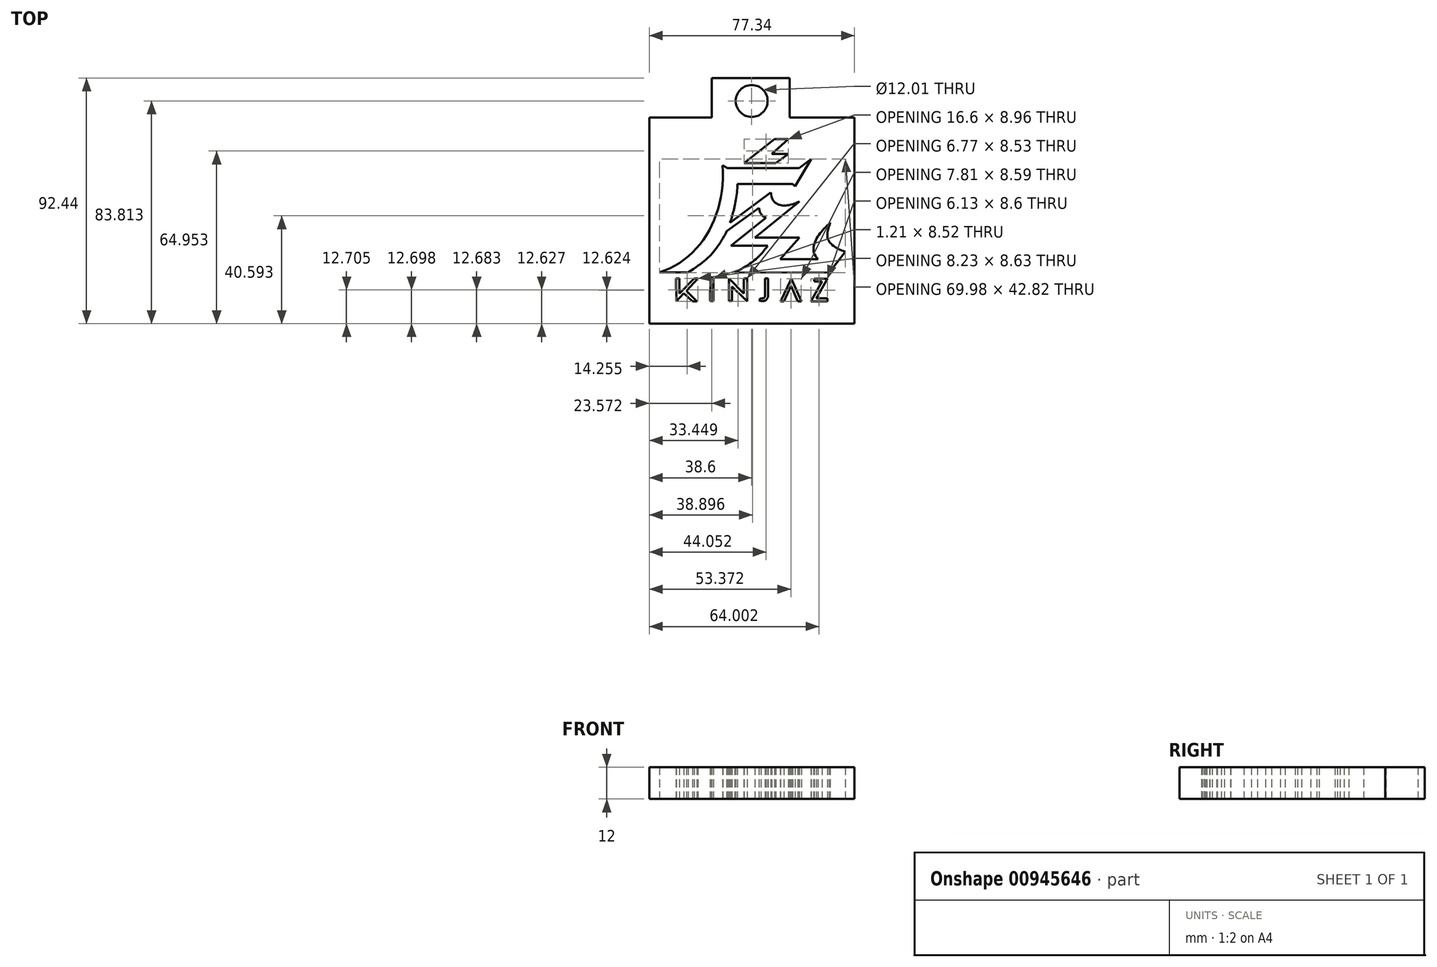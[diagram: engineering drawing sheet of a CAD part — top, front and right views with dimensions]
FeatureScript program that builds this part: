
annotation { "Feature Type Name" : "Feature", "Feature Type Description" : "" }
export const myFeature = defineFeature(function(context is Context, id is Id, definition is map)
    precondition{}
    {
        {
            var Q0;
            Q0=qCreatedBy(makeId("Top.planeOp"),FACE);
            var sketch = newSketch(context, id + "F0", { "sketchPlane" : qUnion([Q0])});
            skLineSegment(sketch, "E0", {"start": v(-62.68, -21.2) * mm, "end": v(-73.43, -21.2) * mm});
            skFitSpline(sketch, "E1", {"points": [v(-73.43, -21.2) * mm, v(-49.68, 19) * mm], "startDerivative": vector(47.19, 15.16) * mm, "endDerivative": vector(-3.26, 57) * mm});
            skLineSegment(sketch, "E2", {"start": v(-49.68, 19) * mm, "end": v(-47.8, 18.08) * mm});
            skLineSegment(sketch, "E3", {"start": v(-47.8, 18.08) * mm, "end": v(-20.92, 18.08) * mm});
            skLineSegment(sketch, "E4", {"start": v(-20.92, 18.08) * mm, "end": v(-16.26, 21.48) * mm});
            skLineSegment(sketch, "E5", {"start": v(-16.26, 21.48) * mm, "end": v(-22.39, 11.17) * mm});
            skLineSegment(sketch, "E6", {"start": v(-22.39, 11.17) * mm, "end": v(-23.32, 12.08) * mm});
            skLineSegment(sketch, "E7", {"start": v(-23.32, 12.08) * mm, "end": v(-44.1, 12.08) * mm});
            skFitSpline(sketch, "E8", {"points": [v(-44.1, 12.08) * mm, v(-46.88, -2.52) * mm], "startDerivative": vector(-0.62, -19.4) * mm, "endDerivative": vector(-2.9, -9.08) * mm});
            skLineSegment(sketch, "E9", {"start": v(-46.88, -2.52) * mm, "end": v(-31.55, 8.9) * mm});
            skFitSpline(sketch, "E10", {"points": [v(-31.55, 8.9) * mm, v(-20.72, 5.45) * mm], "startDerivative": vector(1, -17.55) * mm, "endDerivative": vector(15.07, 7.4) * mm});
            skLineSegment(sketch, "E11", {"start": v(-20.72, 5.45) * mm, "end": v(-37.54, -8.14) * mm});
            skLineSegment(sketch, "E12", {"start": v(-37.54, -8.14) * mm, "end": v(-20.72, -8.14) * mm});
            skLineSegment(sketch, "E13", {"start": v(-20.72, -8.14) * mm, "end": v(-27.98, -16.25) * mm});
            skLineSegment(sketch, "E14", {"start": v(-27.98, -16.25) * mm, "end": v(-13.84, -16.24) * mm});
            skFitSpline(sketch, "E15", {"points": [v(-13.84, -16.24) * mm, v(-9.18, -2.48) * mm], "startDerivative": vector(-12.1, 12.63) * mm, "endDerivative": vector(13.54, 12.46) * mm});
            skFitSpline(sketch, "E16", {"points": [v(-9.18, -2.48) * mm, v(-3.46, -13.46) * mm], "startDerivative": vector(-3.73, -12.22) * mm, "endDerivative": vector(26.55, -9.04) * mm});
            skLineSegment(sketch, "E17", {"start": v(-3.46, -13.46) * mm, "end": v(-9.55, -21.33) * mm});
            skLineSegment(sketch, "E18", {"start": v(-9.55, -21.33) * mm, "end": v(-45.15, -21.17) * mm});
            skFitSpline(sketch, "E19", {"points": [v(-45.15, -21.17) * mm, v(-32.64, -11.13) * mm], "startDerivative": vector(11.27, 5.6) * mm, "endDerivative": vector(13.15, 18.44) * mm});
            skLineSegment(sketch, "E20", {"start": v(-32.64, -11.13) * mm, "end": v(-46.53, -11.13) * mm});
            skLineSegment(sketch, "E21", {"start": v(-46.53, -11.13) * mm, "end": v(-33.3, -0.7) * mm});
            skFitSpline(sketch, "E22", {"points": [v(-35.96, 3.08) * mm, v(-33.3, -0.7) * mm], "startDerivative": vector(0.57, -2.62) * mm, "endDerivative": vector(7.97, -3.11) * mm});
            skLineSegment(sketch, "E23", {"start": v(-35.96, 3.08) * mm, "end": v(-48.13, -5.8) * mm});
            skFitSpline(sketch, "E24", {"points": [v(-48.13, -5.8) * mm, v(-62.68, -21.2) * mm], "startDerivative": vector(-11.33, -21.28) * mm, "endDerivative": vector(-24.18, -14.95) * mm});
            skLineSegment(sketch, "E25", {"start": v(-41.6, 19.95) * mm, "end": v(-29.66, 19.95) * mm});
            skLineSegment(sketch, "E26", {"start": v(-29.66, 19.95) * mm, "end": v(-24.99, 23.3) * mm});
            skLineSegment(sketch, "E27", {"start": v(-24.99, 23.3) * mm, "end": v(-31.19, 23.3) * mm});
            skLineSegment(sketch, "E28", {"start": v(-31.19, 23.3) * mm, "end": v(-24.99, 28.91) * mm});
            skLineSegment(sketch, "E29", {"start": v(-24.99, 28.91) * mm, "end": v(-30.1, 28.91) * mm});
            skLineSegment(sketch, "E30", {"start": v(-30.1, 28.91) * mm, "end": v(-41.6, 19.95) * mm});
            skLineSegment(sketch, "E31", {"start": v(-67.2, -23.56) * mm, "end": v(-66.02, -23.56) * mm});
            skLineSegment(sketch, "E32", {"start": v(-66.02, -23.56) * mm, "end": v(-66.02, -29.19) * mm});
            skLineSegment(sketch, "E33", {"start": v(-66.02, -29.19) * mm, "end": v(-60.45, -23.52) * mm});
            skLineSegment(sketch, "E34", {"start": v(-60.45, -23.52) * mm, "end": v(-58.97, -23.52) * mm});
            skLineSegment(sketch, "E35", {"start": v(-58.97, -23.52) * mm, "end": v(-63.34, -28.2) * mm});
            skLineSegment(sketch, "E36", {"start": v(-63.34, -28.2) * mm, "end": v(-59.36, -32.15) * mm});
            skLineSegment(sketch, "E37", {"start": v(-59.36, -32.15) * mm, "end": v(-61.02, -32.15) * mm});
            skLineSegment(sketch, "E38", {"start": v(-61.02, -32.15) * mm, "end": v(-64.27, -29.08) * mm});
            skLineSegment(sketch, "E39", {"start": v(-64.27, -29.08) * mm, "end": v(-67.16, -32.13) * mm});
            skLineSegment(sketch, "E40", {"start": v(-67.16, -32.13) * mm, "end": v(-67.2, -23.56) * mm});
            skLineSegment(sketch, "E41", {"start": v(-54.3, -23.56) * mm, "end": v(-53.16, -23.56) * mm});
            skLineSegment(sketch, "E42", {"start": v(-53.16, -23.56) * mm, "end": v(-53.16, -32.07) * mm});
            skLineSegment(sketch, "E43", {"start": v(-53.16, -32.07) * mm, "end": v(-54.37, -32.07) * mm});
            skLineSegment(sketch, "E44", {"start": v(-54.37, -32.07) * mm, "end": v(-54.3, -23.56) * mm});
            skLineSegment(sketch, "E45", {"start": v(-47.28, -32.07) * mm, "end": v(-46.14, -32.07) * mm});
            skLineSegment(sketch, "E46", {"start": v(-46.14, -32.07) * mm, "end": v(-46.14, -26.55) * mm});
            skLineSegment(sketch, "E47", {"start": v(-46.14, -26.55) * mm, "end": v(-40.5, -32.09) * mm});
            skLineSegment(sketch, "E48", {"start": v(-40.5, -32.09) * mm, "end": v(-40.5, -23.56) * mm});
            skLineSegment(sketch, "E49", {"start": v(-40.5, -23.56) * mm, "end": v(-41.7, -23.56) * mm});
            skLineSegment(sketch, "E50", {"start": v(-41.7, -23.56) * mm, "end": v(-41.7, -29.19) * mm});
            skLineSegment(sketch, "E51", {"start": v(-41.7, -29.19) * mm, "end": v(-47.25, -23.56) * mm});
            skLineSegment(sketch, "E52", {"start": v(-47.25, -23.56) * mm, "end": v(-47.28, -32.07) * mm});
            skFitSpline(sketch, "E53", {"points": [v(-35.95, -31.8) * mm, v(-32.6, -30.5) * mm], "startDerivative": vector(7.27, -2.05) * mm, "endDerivative": vector(1.5, 3.19) * mm});
            skLineSegment(sketch, "E54", {"start": v(-32.6, -30.5) * mm, "end": v(-32.6, -23.54) * mm});
            skLineSegment(sketch, "E55", {"start": v(-32.6, -23.54) * mm, "end": v(-33.72, -23.54) * mm});
            skLineSegment(sketch, "E56", {"start": v(-33.72, -23.54) * mm, "end": v(-33.72, -30.23) * mm});
            skFitSpline(sketch, "E57", {"points": [v(-33.72, -30.23) * mm, v(-35.23, -30.94) * mm], "startDerivative": vector(-0.8, -2.46) * mm, "endDerivative": vector(-2.36, 0.84) * mm});
            skLineSegment(sketch, "E58", {"start": v(-35.23, -30.94) * mm, "end": v(-35.95, -31.8) * mm});
            skLineSegment(sketch, "E59", {"start": v(-27.87, -32.15) * mm, "end": v(-26.58, -32.15) * mm});
            skLineSegment(sketch, "E60", {"start": v(-26.58, -32.15) * mm, "end": v(-23.92, -26.29) * mm});
            skLineSegment(sketch, "E61", {"start": v(-23.92, -26.29) * mm, "end": v(-21.36, -32.19) * mm});
            skLineSegment(sketch, "E62", {"start": v(-21.36, -32.19) * mm, "end": v(-20.06, -32.19) * mm});
            skLineSegment(sketch, "E63", {"start": v(-20.06, -32.19) * mm, "end": v(-23.86, -23.6) * mm});
            skLineSegment(sketch, "E64", {"start": v(-23.86, -23.6) * mm, "end": v(-27.87, -32.15) * mm});
            skLineSegment(sketch, "E65", {"start": v(-10.27, -32.2) * mm, "end": v(-10.27, -31) * mm});
            skLineSegment(sketch, "E66", {"start": v(-10.27, -31) * mm, "end": v(-14.4, -31) * mm});
            skLineSegment(sketch, "E67", {"start": v(-14.4, -31) * mm, "end": v(-10.27, -23.6) * mm});
            skLineSegment(sketch, "E68", {"start": v(-10.27, -23.6) * mm, "end": v(-15.23, -23.6) * mm});
            skLineSegment(sketch, "E69", {"start": v(-15.23, -23.6) * mm, "end": v(-15.23, -24.7) * mm});
            skLineSegment(sketch, "E70", {"start": v(-15.23, -24.7) * mm, "end": v(-12.2, -24.7) * mm});
            skLineSegment(sketch, "E71", {"start": v(-12.2, -24.7) * mm, "end": v(-16.4, -32.2) * mm});
            skLineSegment(sketch, "E72", {"start": v(-16.4, -32.2) * mm, "end": v(-10.27, -32.2) * mm});
            skLineSegment(sketch, "E73", {"start": v(-77.32, 37.02) * mm, "end": v(0, 37.02) * mm});
            skLineSegment(sketch, "E74", {"start": v(0, 37.02) * mm, "end": v(0, -40.52) * mm});
            skLineSegment(sketch, "E75", {"start": v(0, -40.52) * mm, "end": v(-77.34, -40.52) * mm});
            skLineSegment(sketch, "E76", {"start": v(-77.34, -40.52) * mm, "end": v(-77.32, 37.02) * mm});
            skLineSegment(sketch, "E77", {"start": v(-53.77, 32.2) * mm, "end": v(-24.47, 32.2) * mm});
            skLineSegment(sketch, "E78", {"start": v(-24.47, 32.2) * mm, "end": v(-24.47, 51.92) * mm});
            skLineSegment(sketch, "E79", {"start": v(-24.47, 51.92) * mm, "end": v(-53.77, 51.92) * mm});
            skLineSegment(sketch, "E80", {"start": v(-53.77, 51.92) * mm, "end": v(-53.77, 32.2) * mm});
            skCircle(sketch, "E81", {"center": v(-38.74, 43.3) * mm, "radius": 6 * mm});
            skPoint(sketch, "E82.orphan", {"position": v(-32.5, -11.13) * mm});
            skSolve(sketch);
        }
        {
            var Q0;
            {var subQ0=sQuery(id+"F0.wireOp",EDGE,"E79");Q0=makeQuery(id+"F0.imprint","IMPRINT",FACE,{"disambiguationData":[TD([[makeQuery(id+"F0.imprint","IMPRINT",EDGE,{"derivedFrom":subQ0}),1.0]])]});}
            var Q1;
            {var subQ1=sQuery(id+"F0.wireOp",EDGE,"E77");Q1=makeQuery(id+"F0.imprint","IMPRINT",FACE,{"disambiguationData":[TD([[makeQuery(id+"F0.imprint","IMPRINT",EDGE,{"derivedFrom":subQ1}),1.0]])]});}
            var Q2;
            Q2=makeQuery(id+"F0.imprint","IMPRINT",FACE,{"disambiguationData":[TD([[makeQuery(id+"F0.imprint","IMPRINT",EDGE,{"derivedFrom":sQuery(id+"F0.wireOp",EDGE,"E0")}),1.0]])]});
            extrude(context, id + "F1", {"entities" : qUnion([Q0, Q1, Q2]), "depth" : 12 * mm, "offsetDistance" : 25 * mm});
        }
    });
